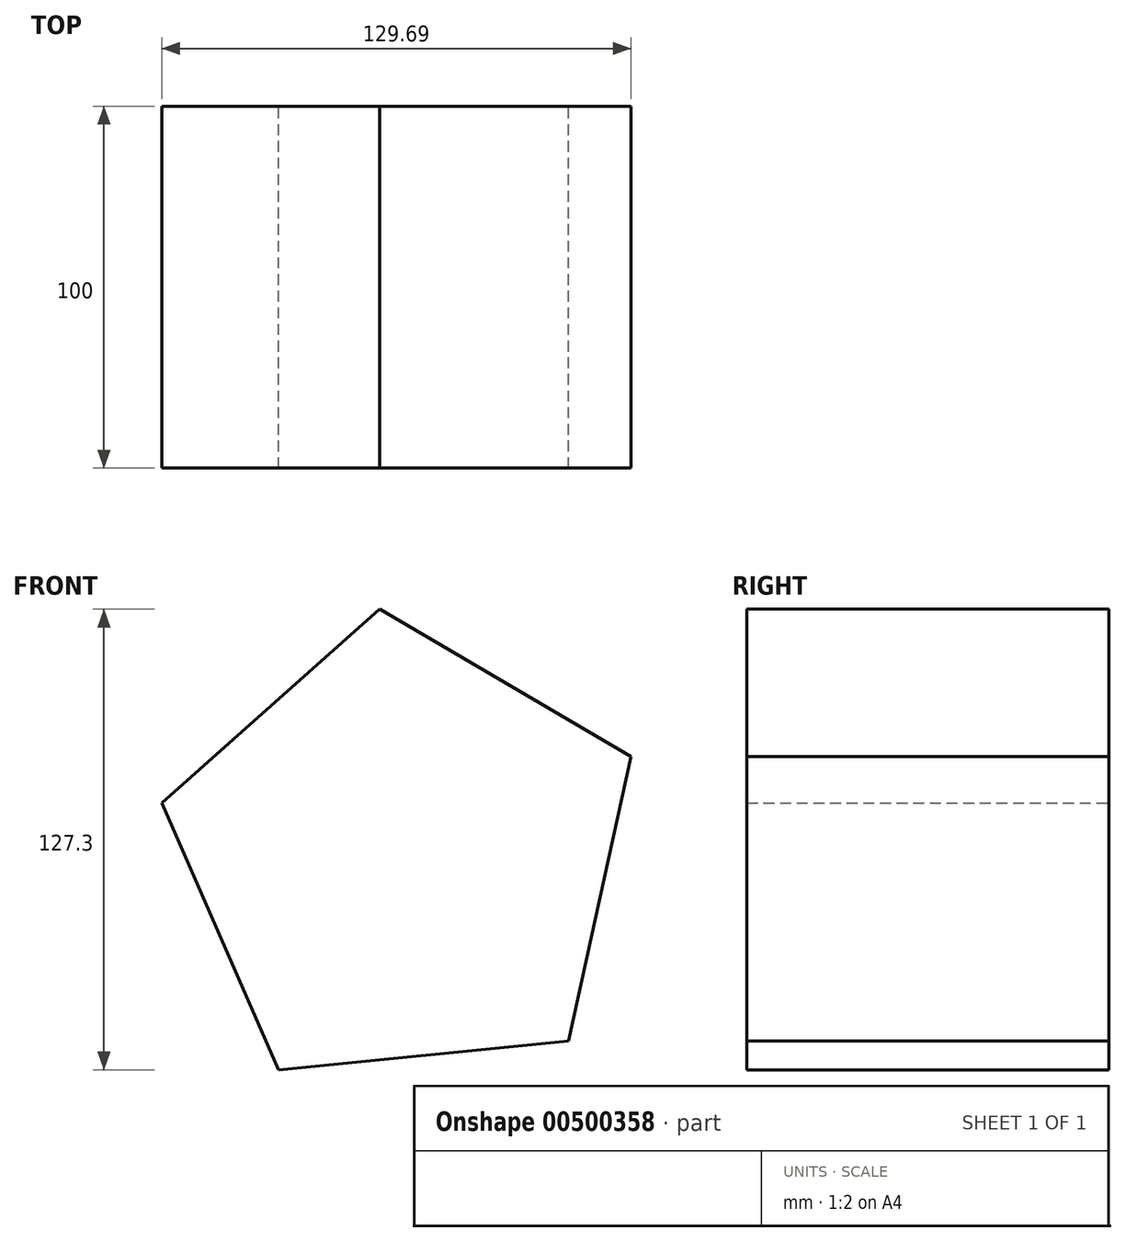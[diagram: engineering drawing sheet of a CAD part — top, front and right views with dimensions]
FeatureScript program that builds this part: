
annotation { "Feature Type Name" : "Feature", "Feature Type Description" : "" }
export const myFeature = defineFeature(function(context is Context, id is Id, definition is map)
    precondition{}
    {
        {
            var Q0;
            Q0=qCreatedBy(makeId("Front.planeOp"),FACE);
            var sketch = newSketch(context, id + "F0", { "sketchPlane" : qUnion([Q0])});
            skCircle(sketch, "E0.cCircle", {"center": v(0, 0) * mm, "radius": 55.43 * mm, "construction": true});
            skLineSegment(sketch, "E0.0", {"start": v(-6.74, 68.18) * mm, "end": v(62.76, 27.48) * mm});
            skLineSegment(sketch, "E0.1", {"start": v(62.76, 27.48) * mm, "end": v(45.53, -51.2) * mm});
            skLineSegment(sketch, "E0.2", {"start": v(45.53, -51.2) * mm, "end": v(-34.62, -59.12) * mm});
            skLineSegment(sketch, "E0.3", {"start": v(-34.62, -59.12) * mm, "end": v(-66.93, 14.66) * mm});
            skLineSegment(sketch, "E0.4", {"start": v(-66.93, 14.66) * mm, "end": v(-6.74, 68.18) * mm});
            skPoint(sketch, "E0.0.midPoint", {"position": v(28.01, 47.83) * mm});
            skSolve(sketch);
        }
        {
            var Q0;
            Q0 = qSketchRegion(id + "F0", true);
            extrude(context, id + "F1", {"entities" : qUnion([Q0]), "depth" : 100 * mm});
        }
    });
